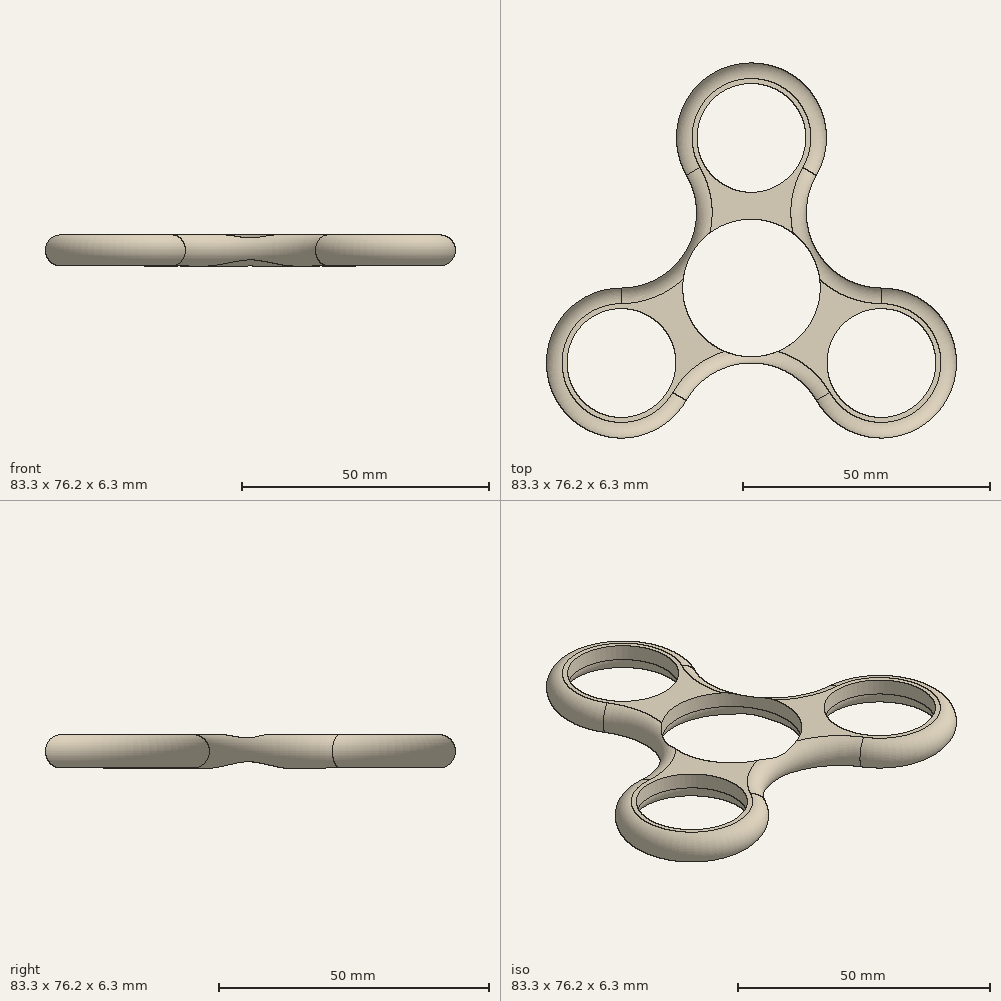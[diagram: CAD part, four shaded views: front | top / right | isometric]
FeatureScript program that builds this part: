
annotation { "Feature Type Name" : "Feature", "Feature Type Description" : "" }
export const myFeature = defineFeature(function(context is Context, id is Id, definition is map)
    precondition{}
    {
        {
            var Q0;
            Q0=qCreatedBy(makeId("Top.planeOp"),FACE);
            var sketch = newSketch(context, id + "F0", { "sketchPlane" : qUnion([Q0])});
            skCircle(sketch, "E0", {"center": v(0, 0) * mm, "radius": 11.05 * mm});
            skCircle(sketch, "E1", {"center": v(0, 0) * mm, "radius": 13.97 * mm});
            skCircle(sketch, "E2", {"center": v(0, 30.48) * mm, "radius": 15.24 * mm});
            skCircle(sketch, "E3", {"center": v(0, 30.48) * mm, "radius": 11.05 * mm});
            skCircle(sketch, "E4.1.0", {"center": v(-26.4, -15.24) * mm, "radius": 15.24 * mm});
            skCircle(sketch, "E4.1.1", {"center": v(-26.4, -15.24) * mm, "radius": 11.05 * mm});
            skCircle(sketch, "E4.2.0", {"center": v(26.4, -15.24) * mm, "radius": 15.24 * mm});
            skCircle(sketch, "E4.2.1", {"center": v(26.4, -15.24) * mm, "radius": 11.05 * mm});
            skArc(sketch, "E5", {"start": v(-26.4, 0) * mm, "mid": v(-13.2, 7.62) * mm, "end": v(-13.2, 22.86) * mm});
            skArc(sketch, "E6.1.0", {"start": v(13.2, -22.86) * mm, "mid": v(0, -15.24) * mm, "end": v(-13.2, -22.86) * mm});
            skArc(sketch, "E6.2.0", {"start": v(13.2, 22.86) * mm, "mid": v(13.2, 7.62) * mm, "end": v(26.4, 0) * mm});
            skSolve(sketch);
        }
        {
            var Q0;
            Q0 = qSketchRegion(id + "F0", true);
            extrude(context, id + "F1", {"entities" : qUnion([Q0]), "depth" : 6.35 * mm, "offsetDistance" : 25.4 * mm});
        }
        {
            var Q0;
            Q0=makeQuery(id+"F1.opExtrude","CAP_EDGE",EDGE,{"disambiguationData":[OSD([sQuery(id+"F0.wireOp",EDGE,"E4.1.0")])],"isStart":false});
            var Q1;
            Q1=makeQuery(id+"F1.opExtrude","CAP_EDGE",EDGE,{"disambiguationData":[OSD([sQuery(id+"F0.wireOp",EDGE,"E5")])],"isStart":false});
            var Q2;
            Q2=makeQuery(id+"F1.opExtrude","CAP_EDGE",EDGE,{"disambiguationData":[OSD([sQuery(id+"F0.wireOp",EDGE,"E6.1.0")])],"isStart":false});
            var Q3;
            Q3=makeQuery(id+"F1.opExtrude","CAP_EDGE",EDGE,{"disambiguationData":[OSD([sQuery(id+"F0.wireOp",EDGE,"E2")])],"isStart":false});
            var Q4;
            Q4=makeQuery(id+"F1.opExtrude","CAP_EDGE",EDGE,{"disambiguationData":[OSD([sQuery(id+"F0.wireOp",EDGE,"E6.2.0")])],"isStart":false});
            var Q5;
            Q5=makeQuery(id+"F1.opExtrude","CAP_EDGE",EDGE,{"disambiguationData":[OSD([sQuery(id+"F0.wireOp",EDGE,"E4.2.0")])],"isStart":false});
            var Q6;
            Q6=makeQuery(id+"F1.opExtrude","CAP_EDGE",EDGE,{"disambiguationData":[OSD([sQuery(id+"F0.wireOp",EDGE,"E6.2.0")])],"isStart":true});
            var Q7;
            Q7=makeQuery(id+"F1.opExtrude","CAP_EDGE",EDGE,{"disambiguationData":[OSD([sQuery(id+"F0.wireOp",EDGE,"E4.2.0")])],"isStart":true});
            var Q8;
            Q8=makeQuery(id+"F1.opExtrude","CAP_EDGE",EDGE,{"disambiguationData":[OSD([sQuery(id+"F0.wireOp",EDGE,"E6.1.0")])],"isStart":true});
            var Q9;
            Q9=makeQuery(id+"F1.opExtrude","CAP_EDGE",EDGE,{"disambiguationData":[OSD([sQuery(id+"F0.wireOp",EDGE,"E4.1.0")])],"isStart":true});
            var Q10;
            Q10=makeQuery(id+"F1.opExtrude","CAP_EDGE",EDGE,{"disambiguationData":[OSD([sQuery(id+"F0.wireOp",EDGE,"E5")])],"isStart":true});
            var Q11;
            Q11=makeQuery(id+"F1.opExtrude","CAP_EDGE",EDGE,{"disambiguationData":[OSD([sQuery(id+"F0.wireOp",EDGE,"E2")])],"isStart":true});
            var Q12;
            Q12=makeQuery(id+"F1.opExtrude","CAP_FACE",FACE,{"disambiguationData":[OSD([sQuery(id+"F0.wireOp",EDGE,"E1"),sQuery(id+"F0.wireOp",EDGE,"E2"),sQuery(id+"F0.wireOp",EDGE,"E3"),sQuery(id+"F0.wireOp",EDGE,"E4.1.0"),sQuery(id+"F0.wireOp",EDGE,"E4.1.1"),sQuery(id+"F0.wireOp",EDGE,"E4.2.0"),sQuery(id+"F0.wireOp",EDGE,"E4.2.1"),sQuery(id+"F0.wireOp",EDGE,"E5"),sQuery(id+"F0.wireOp",EDGE,"E6.1.0"),sQuery(id+"F0.wireOp",EDGE,"E6.2.0")])],"isStart":true});
            fillet(context, id + "F2", {"entities" : qUnion([Q0, Q1, Q2, Q3, Q4, Q5, Q6, Q7, Q8, Q9, Q10, Q11, Q12]), "radius" : 3.17 * mm, "tangentPropagation" : true, "allowEdgeOverflow" : false});
        }
    });
